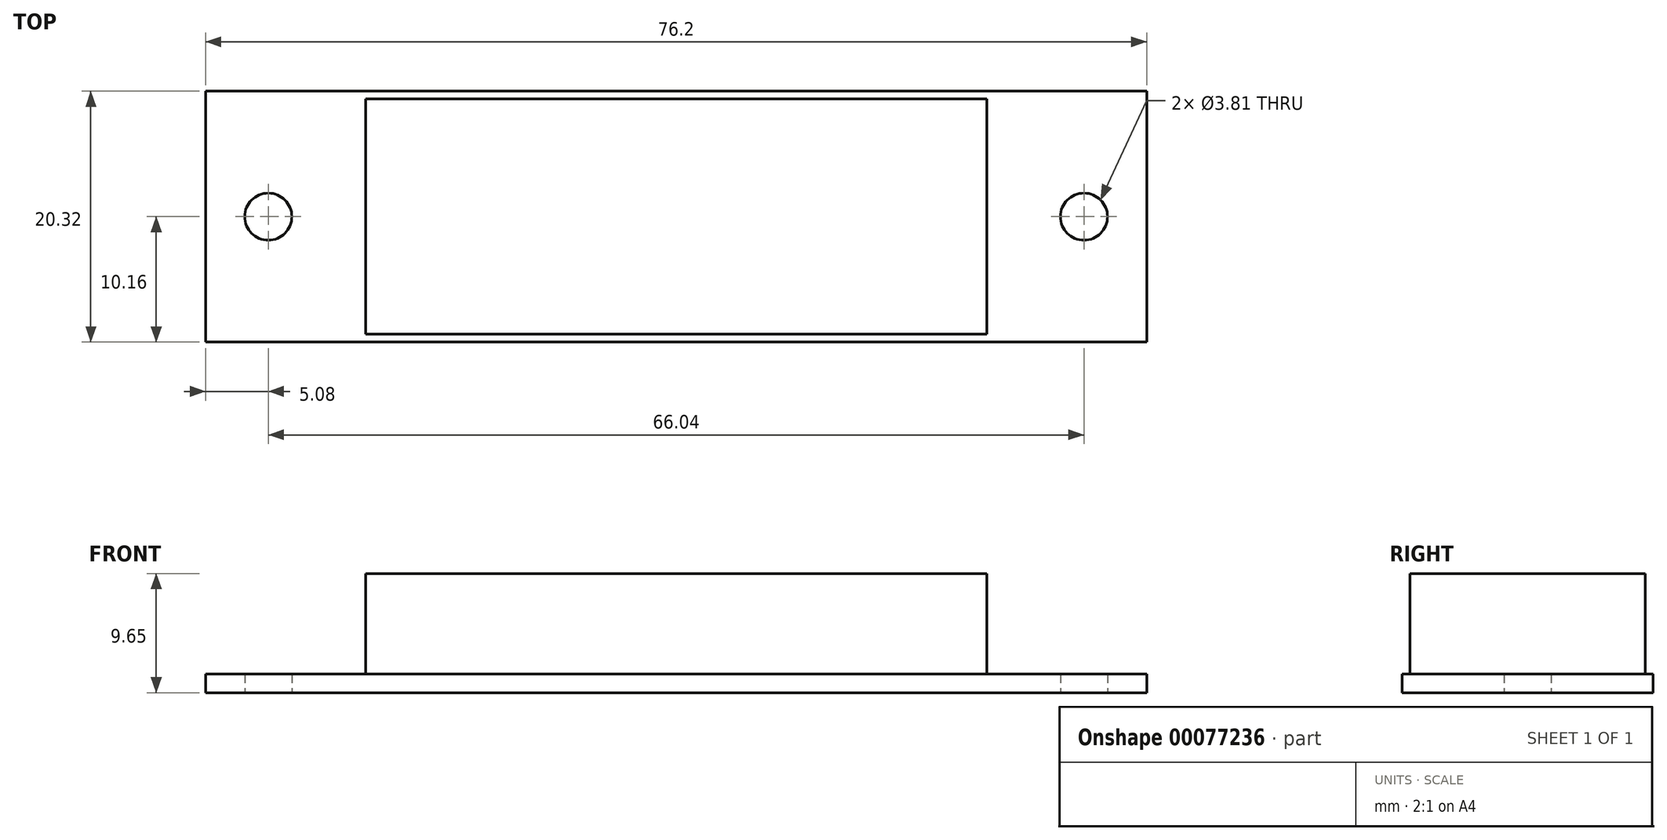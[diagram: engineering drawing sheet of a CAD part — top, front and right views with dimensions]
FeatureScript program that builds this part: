
annotation { "Feature Type Name" : "Feature", "Feature Type Description" : "" }
export const myFeature = defineFeature(function(context is Context, id is Id, definition is map)
    precondition{}
    {
        {
            var Q0;
            Q0=qCreatedBy(makeId("Top.planeOp"),FACE);
            var sketch = newSketch(context, id + "F0", { "sketchPlane" : qUnion([Q0])});
            skLineSegment(sketch, "E0.bottom", {"start": v(-38.1, 10.16) * mm, "end": v(38.1, 10.16) * mm});
            skLineSegment(sketch, "E0.top", {"start": v(-38.1, -10.16) * mm, "end": v(38.1, -10.16) * mm});
            skLineSegment(sketch, "E0.left", {"start": v(-38.1, 10.16) * mm, "end": v(-38.1, -10.16) * mm});
            skLineSegment(sketch, "E0.right", {"start": v(38.1, 10.16) * mm, "end": v(38.1, -10.16) * mm});
            skCircle(sketch, "E1", {"center": v(-33.02, 0) * mm, "radius": 1.9 * mm});
            skCircle(sketch, "E2", {"center": v(33.02, 0) * mm, "radius": 1.9 * mm});
            skLineSegment(sketch, "E3", {"start": v(-38.1, 0) * mm, "end": v(38.1, 0) * mm, "construction": true});
            skSolve(sketch);
        }
        {
            var Q0;
            Q0 = qSketchRegion(id + "F0", true);
            extrude(context, id + "F1", {"entities" : qUnion([Q0]), "depth" : 1.52 * mm});
        }
        {
            var Q0;
            Q0=makeQuery(id+"F1.opExtrude","CAP_FACE",FACE,{"disambiguationData":[OSD([sQuery(id+"F0.wireOp",EDGE,"E0.bottom"),sQuery(id+"F0.wireOp",EDGE,"E0.top"),sQuery(id+"F0.wireOp",EDGE,"E0.left"),sQuery(id+"F0.wireOp",EDGE,"E0.right"),sQuery(id+"F0.wireOp",EDGE,"E1"),sQuery(id+"F0.wireOp",EDGE,"E2")])],"isStart":false});
            var sketch = newSketch(context, id + "F2", { "sketchPlane" : qUnion([Q0])});
            skLineSegment(sketch, "E4.bottom", {"start": v(-25.15, 9.53) * mm, "end": v(25.15, 9.53) * mm});
            skLineSegment(sketch, "E4.top", {"start": v(-25.15, -9.52) * mm, "end": v(25.15, -9.52) * mm});
            skLineSegment(sketch, "E4.left", {"start": v(-25.15, 9.52) * mm, "end": v(-25.15, -9.52) * mm});
            skLineSegment(sketch, "E4.right", {"start": v(25.15, 9.52) * mm, "end": v(25.15, -9.52) * mm});
            skLineSegment(sketch, "E5", {"start": v(-25.15, 0) * mm, "end": v(-38.1, 0) * mm, "construction": true});
            skLineSegment(sketch, "E6", {"start": v(25.15, 0) * mm, "end": v(38.1, 0) * mm, "construction": true});
            skSolve(sketch);
        }
        {
            var Q0;
            Q0=makeQuery(id+"F2.imprint","IMPRINT",FACE,{"disambiguationData":[TD([[makeQuery(id+"F2.imprint","IMPRINT",EDGE,{"derivedFrom":sQuery(id+"F2.wireOp",EDGE,"E4.bottom")}),-1.0]])]});
            extrude(context, id + "F3", {"entities" : qUnion([Q0]), "operationType" : NewBodyOperationType.ADD, "depth" : 8.13 * mm});
        }
        {
            var Q0;
            Q0=qCreatedBy(makeId("Top.planeOp"),FACE);
            var sketch = newSketch(context, id + "F4", { "sketchPlane" : qUnion([Q0])});
            skLineSegment(sketch, "E7.bottom", {"start": v(28.9, 24.42) * mm, "end": v(82.37, 24.42) * mm});
            skLineSegment(sketch, "E7.top", {"start": v(28.9, 60.24) * mm, "end": v(82.37, 60.24) * mm});
            skLineSegment(sketch, "E7.left", {"start": v(28.9, 24.42) * mm, "end": v(28.9, 60.24) * mm});
            skLineSegment(sketch, "E7.right", {"start": v(82.37, 24.42) * mm, "end": v(82.37, 60.24) * mm});
            skCircle(sketch, "E8", {"center": v(33.99, 40.93) * mm, "radius": 1.9 * mm});
            skLineSegment(sketch, "E9", {"start": v(33.99, 40.93) * mm, "end": v(72.09, 40.93) * mm, "construction": true});
            skCircle(sketch, "E10", {"center": v(72.09, 40.93) * mm, "radius": 1.9 * mm});
            skSolve(sketch);
        }
        {
            var Q0;
            Q0 = qSketchRegion(id + "F4", true);
            extrude(context, id + "F5", {"entities" : qUnion([Q0]), "depth" : 1.6 * mm});
        }
        {
            var Q0;
            Q0=makeQuery(id+"F5.opExtrude","CAP_FACE",FACE,{"disambiguationData":[OSD([sQuery(id+"F4.wireOp",EDGE,"E7.bottom"),sQuery(id+"F4.wireOp",EDGE,"E7.top"),sQuery(id+"F4.wireOp",EDGE,"E7.left"),sQuery(id+"F4.wireOp",EDGE,"E7.right"),sQuery(id+"F4.wireOp",EDGE,"E8"),sQuery(id+"F4.wireOp",EDGE,"E10")])],"isStart":false});
            var sketch = newSketch(context, id + "F6", { "sketchPlane" : qUnion([Q0])});
            skLineSegment(sketch, "E11.bottom", {"start": v(40.34, 46.01) * mm, "end": v(65.74, 46.01) * mm});
            skLineSegment(sketch, "E11.top", {"start": v(40.34, 35.85) * mm, "end": v(65.74, 35.85) * mm});
            skLineSegment(sketch, "E11.left", {"start": v(40.34, 46.01) * mm, "end": v(40.34, 35.85) * mm});
            skLineSegment(sketch, "E11.right", {"start": v(65.74, 46.01) * mm, "end": v(65.74, 35.85) * mm});
            skLineSegment(sketch, "E12", {"start": v(40.34, 40.93) * mm, "end": v(33.99, 40.93) * mm, "construction": true});
            skSolve(sketch);
        }
        {
            var Q0;
            Q0 = qSketchRegion(id + "F6", true);
            extrude(context, id + "F7", {"entities" : qUnion([Q0]), "operationType" : NewBodyOperationType.ADD, "depth" : 8.13 * mm});
        }
        {
            var Q0;
            Q0=qCreatedBy(makeId("Top.planeOp"),FACE);
            var sketch = newSketch(context, id + "F8", { "sketchPlane" : qUnion([Q0])});
            skLineSegment(sketch, "E13.bottom", {"start": v(37.04, -66.03) * mm, "end": v(97.04, -66.03) * mm});
            skLineSegment(sketch, "E13.top", {"start": v(37.04, -2.03) * mm, "end": v(97.04, -2.03) * mm});
            skLineSegment(sketch, "E13.left", {"start": v(34.54, -63.53) * mm, "end": v(34.54, -4.53) * mm});
            skLineSegment(sketch, "E13.right", {"start": v(99.54, -63.53) * mm, "end": v(99.54, -4.53) * mm});
            skCircle(sketch, "E14", {"center": v(37.04, -4.53) * mm, "radius": 1.15 * mm});
            skCircle(sketch, "E15", {"center": v(37.04, -63.53) * mm, "radius": 1.15 * mm});
            skCircle(sketch, "E16", {"center": v(97.04, -63.53) * mm, "radius": 1.15 * mm});
            skCircle(sketch, "E17", {"center": v(97.04, -4.53) * mm, "radius": 1.15 * mm});
            skPoint(sketch, "E18.visualSharp", {"position": v(34.54, -2.03) * mm});
            skArc(sketch, "E18.filletArc", {"start": v(37.04, -2.03) * mm, "mid": v(35.27, -2.76) * mm, "end": v(34.54, -4.53) * mm});
            skPoint(sketch, "E19.visualSharp", {"position": v(34.54, -66.03) * mm});
            skArc(sketch, "E19.filletArc", {"start": v(34.54, -63.53) * mm, "mid": v(35.27, -65.3) * mm, "end": v(37.04, -66.03) * mm});
            skPoint(sketch, "E20.visualSharp", {"position": v(99.54, -66.03) * mm});
            skArc(sketch, "E20.filletArc", {"start": v(97.04, -66.03) * mm, "mid": v(98.81, -65.3) * mm, "end": v(99.54, -63.53) * mm});
            skPoint(sketch, "E21.visualSharp", {"position": v(99.54, -2.03) * mm});
            skArc(sketch, "E21.filletArc", {"start": v(99.54, -4.53) * mm, "mid": v(98.81, -2.76) * mm, "end": v(97.04, -2.03) * mm});
            skLineSegment(sketch, "E22", {"start": v(37.04, -4.53) * mm, "end": v(97.04, -4.53) * mm, "construction": true});
            skLineSegment(sketch, "E23", {"start": v(97.04, -63.53) * mm, "end": v(97.04, -4.53) * mm, "construction": true});
            skLineSegment(sketch, "E24", {"start": v(97.04, -63.53) * mm, "end": v(37.04, -63.53) * mm, "construction": true});
            skLineSegment(sketch, "E25", {"start": v(37.04, -63.53) * mm, "end": v(37.04, -4.53) * mm, "construction": true});
            skLineSegment(sketch, "E26", {"start": v(67.04, -4.53) * mm, "end": v(67.04, -2.03) * mm, "construction": true});
            skLineSegment(sketch, "E27", {"start": v(37.04, -34.03) * mm, "end": v(34.54, -34.03) * mm, "construction": true});
            skSolve(sketch);
        }
        {
            var Q0;
            Q0=makeQuery(id+"F8.imprint","IMPRINT",FACE,{"disambiguationData":[TD([[makeQuery(id+"F8.imprint","IMPRINT",EDGE,{"derivedFrom":sQuery(id+"F8.wireOp",EDGE,"E13.bottom")}),1.0]])]});
            extrude(context, id + "F9", {"entities" : qUnion([Q0]), "depth" : 3 * mm});
        }
        {
            var Q0;
            Q0=makeQuery(id+"F9.opExtrude","CAP_FACE",FACE,{"disambiguationData":[OSD([sQuery(id+"F8.wireOp",EDGE,"E13.bottom"),sQuery(id+"F8.wireOp",EDGE,"E13.top"),sQuery(id+"F8.wireOp",EDGE,"E13.left"),sQuery(id+"F8.wireOp",EDGE,"E13.right"),sQuery(id+"F8.wireOp",EDGE,"E14"),sQuery(id+"F8.wireOp",EDGE,"E15"),sQuery(id+"F8.wireOp",EDGE,"E16"),sQuery(id+"F8.wireOp",EDGE,"E17"),sQuery(id+"F8.wireOp",EDGE,"E18.filletArc"),sQuery(id+"F8.wireOp",EDGE,"E19.filletArc"),sQuery(id+"F8.wireOp",EDGE,"E20.filletArc"),sQuery(id+"F8.wireOp",EDGE,"E21.filletArc")])],"isStart":false});
            var sketch = newSketch(context, id + "F10", { "sketchPlane" : qUnion([Q0])});
            skLineSegment(sketch, "E28.bottom", {"start": v(41.04, -5.53) * mm, "end": v(93.04, -5.53) * mm});
            skLineSegment(sketch, "E28.top", {"start": v(41.04, -62.53) * mm, "end": v(93.04, -62.53) * mm});
            skLineSegment(sketch, "E28.left", {"start": v(37.04, -9.53) * mm, "end": v(37.04, -58.53) * mm});
            skLineSegment(sketch, "E28.right", {"start": v(97.04, -9.53) * mm, "end": v(97.04, -58.53) * mm});
            skLineSegment(sketch, "E29", {"start": v(67.04, -5.53) * mm, "end": v(67.04, -2.03) * mm, "construction": true});
            skLineSegment(sketch, "E30", {"start": v(37.04, -34.03) * mm, "end": v(34.54, -34.03) * mm, "construction": true});
            skPoint(sketch, "E31.visualSharp", {"position": v(37.04, -5.53) * mm});
            skArc(sketch, "E31.filletArc", {"start": v(41.04, -5.53) * mm, "mid": v(38.21, -6.7) * mm, "end": v(37.04, -9.53) * mm});
            skPoint(sketch, "E32.visualSharp", {"position": v(37.04, -62.53) * mm});
            skArc(sketch, "E32.filletArc", {"start": v(37.04, -58.53) * mm, "mid": v(38.21, -61.36) * mm, "end": v(41.04, -62.53) * mm});
            skPoint(sketch, "E33.visualSharp", {"position": v(97.04, -62.53) * mm});
            skArc(sketch, "E33.filletArc", {"start": v(93.04, -62.53) * mm, "mid": v(95.87, -61.36) * mm, "end": v(97.04, -58.53) * mm});
            skPoint(sketch, "E34.visualSharp", {"position": v(97.04, -5.53) * mm});
            skArc(sketch, "E34.filletArc", {"start": v(97.04, -9.53) * mm, "mid": v(95.87, -6.7) * mm, "end": v(93.04, -5.53) * mm});
            skSolve(sketch);
        }
        {
            var Q0;
            Q0 = qSketchRegion(id + "F10", true);
            extrude(context, id + "F11", {"entities" : qUnion([Q0]), "operationType" : NewBodyOperationType.ADD, "depth" : 3.6 * mm});
        }
        {
            var Q0;
            Q0=makeQuery(id+"F9.opExtrude","CAP_FACE",FACE,{"disambiguationData":[OSD([sQuery(id+"F8.wireOp",EDGE,"E13.bottom"),sQuery(id+"F8.wireOp",EDGE,"E13.top"),sQuery(id+"F8.wireOp",EDGE,"E13.left"),sQuery(id+"F8.wireOp",EDGE,"E13.right"),sQuery(id+"F8.wireOp",EDGE,"E14"),sQuery(id+"F8.wireOp",EDGE,"E15"),sQuery(id+"F8.wireOp",EDGE,"E16"),sQuery(id+"F8.wireOp",EDGE,"E17"),sQuery(id+"F8.wireOp",EDGE,"E18.filletArc"),sQuery(id+"F8.wireOp",EDGE,"E19.filletArc"),sQuery(id+"F8.wireOp",EDGE,"E20.filletArc"),sQuery(id+"F8.wireOp",EDGE,"E21.filletArc")])],"isStart":true});
            var sketch = newSketch(context, id + "F12", { "sketchPlane" : qUnion([Q0])});
            skLineSegment(sketch, "E35.bottom", {"start": v(42.04, 71.03) * mm, "end": v(92.04, 71.03) * mm});
            skLineSegment(sketch, "E35.top", {"start": v(42.04, 66.03) * mm, "end": v(92.04, 66.03) * mm});
            skLineSegment(sketch, "E35.left", {"start": v(42.04, 71.03) * mm, "end": v(42.04, 66.03) * mm});
            skLineSegment(sketch, "E35.right", {"start": v(92.04, 71.03) * mm, "end": v(92.04, 66.03) * mm});
            skLineSegment(sketch, "E36", {"start": v(67.04, 71.03) * mm, "end": v(67.04, 2.03) * mm});
            skSolve(sketch);
        }
        {
            var Q0;
            {var subQ0=sQuery(id+"F12.wireOp",EDGE,"E35.left");Q0=makeQuery(id+"F12.imprint","IMPRINT",FACE,{"disambiguationData":[TD([[makeQuery(id+"F12.imprint","IMPRINT",EDGE,{"derivedFrom":subQ0}),1.0]])]});}
            var Q1;
            {var subQ0=sQuery(id+"F12.wireOp",EDGE,"E35.right");Q1=makeQuery(id+"F12.imprint","IMPRINT",FACE,{"disambiguationData":[TD([[makeQuery(id+"F12.imprint","IMPRINT",EDGE,{"derivedFrom":subQ0}),-1.0]])]});}
            extrude(context, id + "F13", {"entities" : qUnion([Q0, Q1]), "operationType" : NewBodyOperationType.ADD, "oppositeDirection" : true, "depth" : 1.6 * mm});
        }
        {
            var Q0;
            Q0=makeQuery(id+"F5.opExtrude","SWEPT_BODY",BODY,{"disambiguationData":[OSD([sQuery(id+"F4.wireOp",EDGE,"E7.bottom"),sQuery(id+"F4.wireOp",EDGE,"E7.top"),sQuery(id+"F4.wireOp",EDGE,"E7.left"),sQuery(id+"F4.wireOp",EDGE,"E7.right"),sQuery(id+"F4.wireOp",EDGE,"E8"),sQuery(id+"F4.wireOp",EDGE,"E10")])]});
            deleteBodies(context, id + "F14", {"entities" : qUnion([Q0])});
        }
        {
            var Q0;
            Q0=makeQuery(id+"F9.opExtrude","SWEPT_BODY",BODY,{"disambiguationData":[OSD([sQuery(id+"F8.wireOp",EDGE,"E13.bottom"),sQuery(id+"F8.wireOp",EDGE,"E13.top"),sQuery(id+"F8.wireOp",EDGE,"E13.left"),sQuery(id+"F8.wireOp",EDGE,"E13.right"),sQuery(id+"F8.wireOp",EDGE,"E14"),sQuery(id+"F8.wireOp",EDGE,"E15"),sQuery(id+"F8.wireOp",EDGE,"E16"),sQuery(id+"F8.wireOp",EDGE,"E17"),sQuery(id+"F8.wireOp",EDGE,"E18.filletArc"),sQuery(id+"F8.wireOp",EDGE,"E19.filletArc"),sQuery(id+"F8.wireOp",EDGE,"E20.filletArc"),sQuery(id+"F8.wireOp",EDGE,"E21.filletArc")])]});
            deleteBodies(context, id + "F15", {"entities" : qUnion([Q0])});
        }
    });
